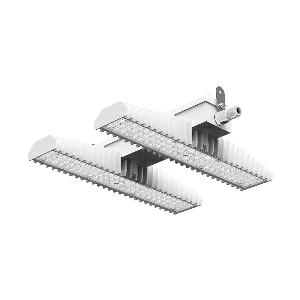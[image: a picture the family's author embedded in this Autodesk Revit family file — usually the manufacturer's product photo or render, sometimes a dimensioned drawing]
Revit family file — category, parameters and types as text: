
# Revit family: 3f_filippi_-_3f_lem_ho_ampio_3f_filippi_-_58972_-_3f_lem_2_ho_led_140_dali_cr_ampio
name_source: partatom
category: Lighting Fixtures
units: mm (PartAtom-declared; Revit-internal decimal feet)

## family parameters
Cut with Voids When Loaded = No
Host = Face
Light Source = No
Part Type = Normal
Room Calculation Point = No
Round Connector Dimension = Use Diameter
Shared = No

## types (1)
- 3F Filippi - 3F LEM HO Ampio (1 x LED, 22606 lm, 138 W, 4000 K)
    Apparent Load = 138 VA
    Approval mark = CE
    CIE Flux Codes = 60 92 99 100 100
    Color Rendering = 80
    Color Temperature = 4000 K
    Control Gear = Electronic transformer
    Default Elevation = 1800 mm
    Description = Industrial luminaire with high light output and high luminous efficiency designed with the most innovative technologies for environments with temperature up to 55°C.

ILLUMINOTECHNICAL
Luminous efficiency 100% (DLOR 100%, ULOR 0%).
Initial luminous flux of the luminaire 22606 lm.
Direct symmetric wide distribution: the illuminated area has a rectangular shape.
Installation Interdistance Transv.D = 1.58 x hu - Long.D = 1.45 x hu.
Tabular UGR (CIE 117 - 4H-8H; S=0.25H; 70/50/20): RUG 23.5 - 24.5.
Beam angle: 93° - 99°.
Luminous efficacy 164 lm/W.
Lifetime (L93/B10): 30000 h. (tq+25°C)
Lifetime (L90/B10): 50000 h. (tq+25°C)
Lifetime (L85/B10): 80000 h. (tq+25°C)
Lifetime (L80/B10): 100000 h. (tq+25°C)
Lifetime (L85/B10): 50000 h. (tq+55°C)
Sudden decreased luminous flux after 50000 hours: 0% (C0).
Photobiological safety in compliance with IEC/TR 62778: RG0 risk exempt, (IEC 62471).
In compliance with IEC/EN 62722-2-1 - IEC/EN 62717 standards.

SOURCE
2 Mid-Power linear LED modules 70W/840.
Energy efficiency class (UE 2019/2020 - UE 2019/2015): C.
CIE 13.3 Colour rendering index: CRI >80 (R9 <50%).
IES TM-30 Fidelity Index: Rf = 84 Rg = 95.
CCT nominal colour temperature 4000 K.
Colour initial tolerance (MacAdam): SDCM 3.

MECHANICAL
Passive modular heatsinks in die-casted aluminium, painted in white colour.
To optimize the thermal management of the LED module, the heatsinks are oversized and provided with self-cleaning of cooling fins.
Wiring body in aluminium and galvanised steel anchored solidly to the sinks and thermally separated.
3F Lens lenses with high luminous efficiency, transparent methacrylate (PMMA), fixed to the LED modules.
Fixing brackets in stainless steel.
Luminaire with limited surface temperature. - D - (EN 60598-2-24)
Dimensions: 470x542 mm, height 129 mm. Weight 9.24 kg.
IP65 protection degree.
Mechanical strength to impacts IK06 (1 joule).
Glow-wire test resistance 650°C.

ELECTRICAL
Halogen Free DALI-2 DATI (Parts 251, 252, 253), PUSH-DIM, electronic wiring 230V-50/60Hz, power factor 0.97 at full load, THD <25%, constant output current, class I, 1 driver, 1 DALI addresse.
Power of the luminaire 138 W.
ENEC - CE.
Flicker: <4%.
Luminaire compliant with EN 60598-2-22 for power supply from a centralised emergency system CPSS (Central Power Supply System), not incorporated in the luminaire - high risk areas excluded. The default power and flux are 100% in AC and 15% in DC.
Ambient temperature from -30°C to +55°C.
Temperature class T6 max 85°C.
Quick connection via M25 5P connector with 9-13 mm tightening range.
Power unit positioned on a separate compartment by the LED module to ensure optimum temperatures of cabling components, to be inspectable and maintainable.
Relative humidity UR: <85%.

INSTALLATION
Ceiling / Suspended / Wall.
All accessories dedicated to this product are available on the Catalog and on our website www.3F-Filippi.com.

APPLICATIONS
In commercial environments, exhibition and industrial areas, stores, open areas.
Environments in which it is necessary a total protection against falling fragments (eg environments with foodstuffs or machines with moving parts or with extreme temperature changes), use luminaires with polycarbonate lenses.

LIGHT MANAGEMENT
Recommended minimum setting: 10%.
The luminaire, equipped with (DALI-2 DATI) driver, can be controlled manually with 3F Easy Dim technology or automatically/manually with wired or wireless DALI/D2D control systems.
The D2D driver guarantees interoperability with other devices with the same certification by making the following information available:
Device Data (Part 251), Energy Report (Part 252), Diagnosis & Maintenance (Part 253).
In electrical systems without a regulation system (manual or automatic) and DALI bus, a suitable jumper must be made on the DA-DA terminals of the appliance.

WARNING
Fixture not suitable for cold stores with an ambient temperature <0°C and/or relative humidity >85%.
Luminaire designed for disposal/recycling at end-of-life.
Replaceable (LED only) light source by a professional. Replaceable control gear by a professional.
    Height = 129 mm
    Lamp = 1 x LED
    Lamp Light Flux = 22606 lm
    Lamp Power = 138 W
    Lamp count = 1
    Length = 470 mm
    Lifetime = 50000 h
    Luminous efficacy = 164 lm/W
    Manufacturer = 3F Filippi
    ModVariant = No
    Model = 3F Filippi - 58972 - 3F LEM 2 HO LED 140 DALI CR AMPIO
    Mounting Place = Ceiling
    Mounting Type = Pendant
    Number of Poles = 1
    OnlyDefault = Yes
    Power Factor = 1
    Product Name = 3F Filippi - 3F LEM HO Ampio
    Product group = pendant luminaire
    ProductGroupID = 9
    Protection Class = Protection class I
    Protection Degree = IP 65
    RLX_Detail_Level = 1
    RLX_Emergency_Light_Flux = 0 lm
    RLX_Emergency_Type = 0
    RLX_Emergency_Type_DB = No
    RlxData = <blob elided: 98329 chars, md5=4c2fb48c>
    Socket = socket
    Standby Power = 0 W
    System Light Flux = 22606 lm
    System Power = 138 W
    Type Comments = Product without accessories
    Type Image = 3f_filippi_-_lem_2.jpg
    URL = http://relux.com
    VarID = ---
    Voltage = 0 V
    Weight = 0.00 kg
    Width = 542 mm

## geometry (parser evidence)
native form markers: Blend x4, Sweep x11
no freeform markers — native parametric forms only
